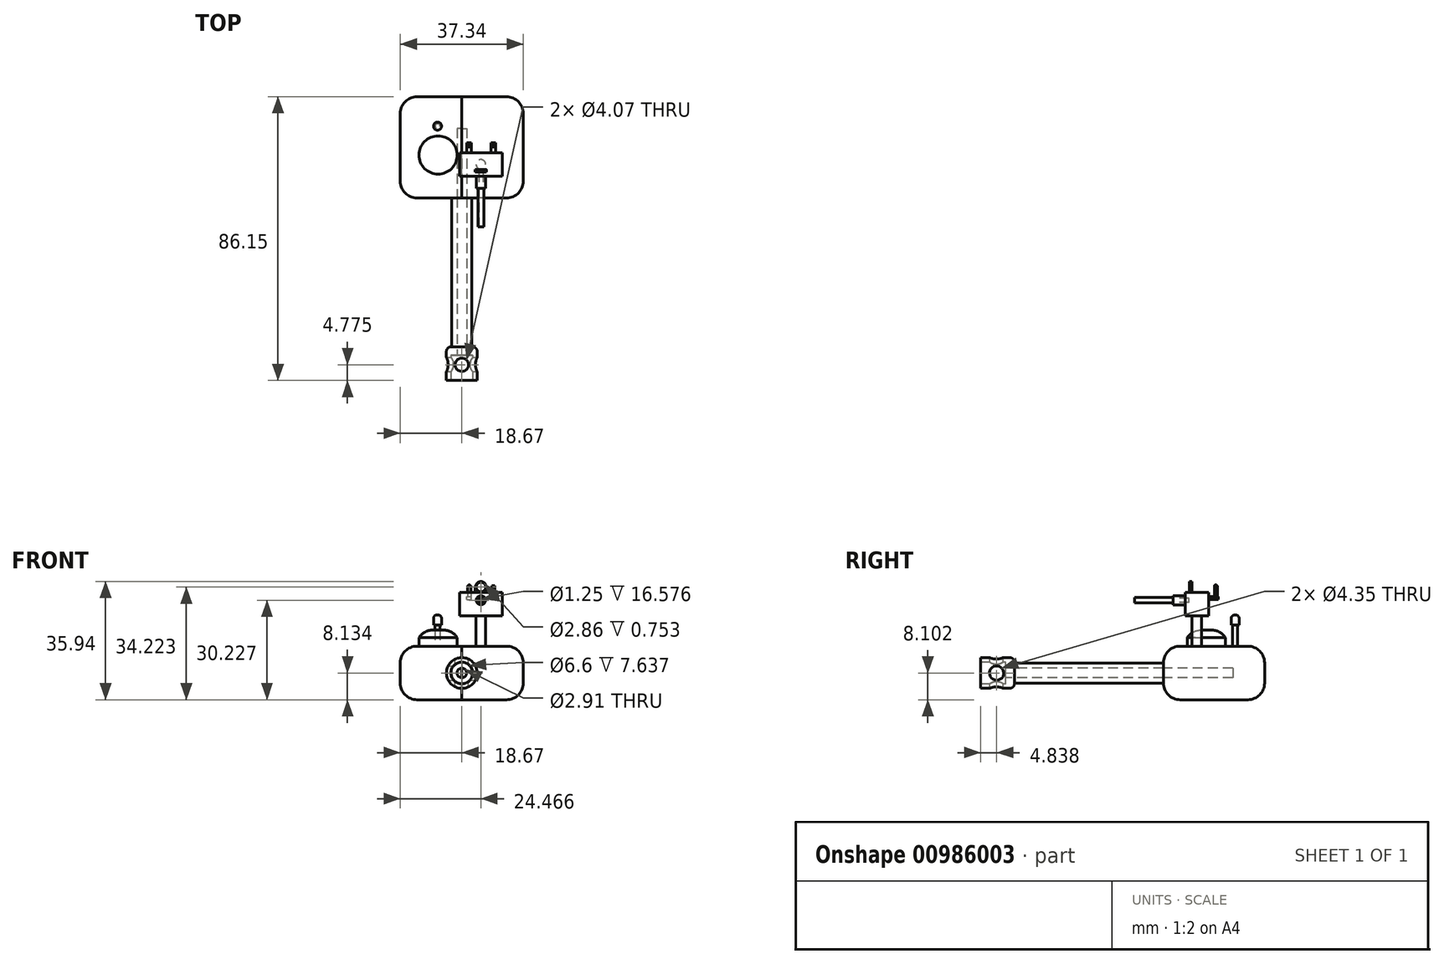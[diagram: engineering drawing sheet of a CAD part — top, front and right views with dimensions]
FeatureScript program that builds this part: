
annotation { "Feature Type Name" : "Feature", "Feature Type Description" : "" }
export const myFeature = defineFeature(function(context is Context, id is Id, definition is map)
    precondition{}
    {
        {
            var Q0;
            Q0=qCreatedBy(makeId("Top.planeOp"),FACE);
            var sketch = newSketch(context, id + "F0", { "sketchPlane" : qUnion([Q0])});
            skLineSegment(sketch, "E0.bottom", {"start": v(27.35, 36.84) * mm, "end": v(45.64, 36.84) * mm});
            skLineSegment(sketch, "E0.top", {"start": v(27.35, -37.1) * mm, "end": v(45.64, -37.1) * mm});
            skLineSegment(sketch, "E0.left", {"start": v(27.35, 36.84) * mm, "end": v(27.35, -37.1) * mm});
            skLineSegment(sketch, "E0.right", {"start": v(45.64, 36.84) * mm, "end": v(45.64, -37.1) * mm});
            skSolve(sketch);
        }
        {
            var Q0;
            Q0=makeQuery(id+"F0.imprint","IMPRINT",FACE,{"disambiguationData":[TD([[makeQuery(id+"F0.imprint","IMPRINT",EDGE,{"derivedFrom":sQuery(id+"F0.wireOp",EDGE,"E0.bottom")}),-1.0]])]});
            extrude(context, id + "F1", {"entities" : qUnion([Q0]), "depth" : 28.5 * mm, "offsetDistance" : 25.4 * mm});
        }
        {
            var Q0;
            Q0=makeQuery(id+"F1.opExtrude","SWEPT_FACE",FACE,{"disambiguationData":[OSD([sQuery(id+"F0.wireOp",EDGE,"E0.top")])]});
            extrude(context, id + "F2", {"entities" : qUnion([Q0]), "operationType" : NewBodyOperationType.ADD, "depth" : 18.17 * mm, "offsetDistance" : 25.4 * mm});
        }
        {
            var Q0;
            {var subQ0=sQuery(id+"F0.wireOp",EDGE,"E0.top");Q0=makeQuery(id+"F2.opExtrude","CAP_EDGE",EDGE,{"disambiguationData":[OSD([subQ0]),TDD([makeQuery(id+"F1.opExtrude","CAP_EDGE",EDGE,{"disambiguationData":[OSD([subQ0])],"isStart":true})])],"isStart":false});}
            var Q1;
            {var subQ0=sQuery(id+"F0.wireOp",EDGE,"E0.top");Q1=makeQuery(id+"F2.opExtrude","CAP_EDGE",EDGE,{"disambiguationData":[OSD([subQ0]),TDD([makeQuery(id+"F1.opExtrude","CAP_EDGE",EDGE,{"disambiguationData":[OSD([subQ0])],"isStart":false})])],"isStart":false});}
            fillet(context, id + "F3", {"entities" : qUnion([Q0, Q1]), "radius" : 16.42 * mm, "tangentPropagation" : true, "allowEdgeOverflow" : false});
        }
        {
            var Q0;
            Q0=makeQuery(id+"F1.opExtrude","SWEPT_BODY",BODY,{"disambiguationData":[OSD([sQuery(id+"F0.wireOp",EDGE,"E0.bottom"),sQuery(id+"F0.wireOp",EDGE,"E0.top"),sQuery(id+"F0.wireOp",EDGE,"E0.left"),sQuery(id+"F0.wireOp",EDGE,"E0.right")])]});
            var Q1;
            Q1=qCreatedBy(makeId("Front.planeOp"),FACE);
            mirror(context, id + "F4", {"operationType" : NewBodyOperationType.ADD, "entities" : qUnion([Q0]), "mirrorPlane" : qUnion([Q1])});
        }
        {
            var Q0;
            {var subQ0=sQuery(id+"F0.wireOp",EDGE,"E0.top");var subQ1=makeQuery(id+"F2.boolean.opBoolean","MERGE",FACE,{"derivedFrom":[makeQuery(id+"F1.opExtrude","CAP_FACE",FACE,{"disambiguationData":[OSD([sQuery(id+"F0.wireOp",EDGE,"E0.bottom"),subQ0,sQuery(id+"F0.wireOp",EDGE,"E0.left"),sQuery(id+"F0.wireOp",EDGE,"E0.right")])],"isStart":false}),makeQuery(id+"F2.opExtrude","SWEPT_FACE",FACE,{"disambiguationData":[OSD([subQ0]),TDD([makeQuery(id+"F1.opExtrude","CAP_EDGE",EDGE,{"disambiguationData":[OSD([subQ0])],"isStart":false})])]})]});Q0=makeQuery(id+"F4.boolean.opBoolean","MERGE",FACE,{"derivedFrom":[subQ1,makeQuery(id+"F4.opPattern","COPY",FACE,{"derivedFrom":subQ1,"instanceName":"1"})]});}
            var sketch = newSketch(context, id + "F5", { "sketchPlane" : qUnion([Q0])});
            skLineSegment(sketch, "E1.bottom", {"start": v(36.5, 38.84) * mm, "end": v(0, 38.84) * mm});
            skLineSegment(sketch, "E1.top", {"start": v(36.5, -38.84) * mm, "end": v(0, -38.84) * mm});
            skLineSegment(sketch, "E1.left", {"start": v(36.5, 38.84) * mm, "end": v(36.5, -38.84) * mm});
            skLineSegment(sketch, "E1.right", {"start": v(0, 38.84) * mm, "end": v(0, -38.84) * mm});
            skSolve(sketch);
        }
        {
            var Q0;
            {var subQ5=sQuery(id+"F5.wireOp",EDGE,"E1.right");Q0=makeQuery(id+"F5.imprint","IMPRINT",FACE,{"disambiguationData":[TD([[makeQuery(id+"F5.imprint","IMPRINT",EDGE,{"derivedFrom":subQ5}),1.0]])]});}
            var Q1;
            {var subQ5=sQuery(id+"F5.wireOp",EDGE,"E1.left");Q1=makeQuery(id+"F5.imprint","IMPRINT",FACE,{"disambiguationData":[TD([[makeQuery(id+"F5.imprint","IMPRINT",EDGE,{"derivedFrom":subQ5}),-1.0]])]});}
            extrude(context, id + "F6", {"entities" : qUnion([Q0, Q1]), "depth" : 15.55 * mm, "offsetDistance" : 25.4 * mm});
        }
        {
            var Q0;
            Q0=makeQuery(id+"F6.opExtrude","CAP_EDGE",EDGE,{"disambiguationData":[OSD([sQuery(id+"F5.wireOp",EDGE,"E1.top")])],"isStart":false});
            fillet(context, id + "F7", {"entities" : qUnion([Q0]), "radius" : 16.9 * mm, "tangentPropagation" : true, "allowEdgeOverflow" : false});
        }
        {
            var Q0;
            Q0=makeQuery(id+"F6.opExtrude","CAP_FACE",FACE,{"disambiguationData":[OSD([sQuery(id+"F5.wireOp",EDGE,"E1.bottom"),sQuery(id+"F5.wireOp",EDGE,"E1.top"),sQuery(id+"F5.wireOp",EDGE,"E1.left"),sQuery(id+"F5.wireOp",EDGE,"E1.right")])],"isStart":false});
            var sketch = newSketch(context, id + "F8", { "sketchPlane" : qUnion([Q0])});
            skLineSegment(sketch, "E2.bottom", {"start": v(36.5, 38.84) * mm, "end": v(0, 38.84) * mm});
            skLineSegment(sketch, "E2.top", {"start": v(36.5, 0) * mm, "end": v(0, 0) * mm});
            skLineSegment(sketch, "E2.left", {"start": v(36.5, 38.84) * mm, "end": v(36.5, 0) * mm});
            skLineSegment(sketch, "E2.right", {"start": v(0, 38.84) * mm, "end": v(0, 0) * mm});
            skSolve(sketch);
        }
        {
            var Q0;
            Q0=makeQuery(id+"F8.imprint","IMPRINT",FACE,{"disambiguationData":[TD([[makeQuery(id+"F8.imprint","IMPRINT",EDGE,{"derivedFrom":sQuery(id+"F8.wireOp",EDGE,"E2.bottom")}),1.0]])]});
            extrude(context, id + "F9", {"entities" : qUnion([Q0]), "operationType" : NewBodyOperationType.ADD, "depth" : 10.94 * mm, "offsetDistance" : 25.4 * mm});
        }
        {
            var Q0;
            Q0=makeQuery(id+"F9.opExtrude","CAP_EDGE",EDGE,{"disambiguationData":[OSD([sQuery(id+"F8.wireOp",EDGE,"E2.top")])],"isStart":false});
            fillet(context, id + "F10", {"entities" : qUnion([Q0]), "radius" : 179.02 * mm, "tangentPropagation" : true, "allowEdgeOverflow" : false});
        }
        {
            var Q0;
            Q0=makeQuery(id+"F10.opFillet","BLEND_EDGE",EDGE,{"blendedFrom":[makeQuery(id+"F9.opExtrude","CAP_EDGE",EDGE,{"disambiguationData":[OSD([sQuery(id+"F8.wireOp",EDGE,"E2.top")])],"isStart":false}),makeQuery(id+"F9.boolean.opBoolean","MERGE",FACE,{"derivedFrom":[makeQuery(id+"F6.opExtrude","SWEPT_FACE",FACE,{"disambiguationData":[OSD([sQuery(id+"F5.wireOp",EDGE,"E1.bottom")])]}),makeQuery(id+"F9.opExtrude","SWEPT_FACE",FACE,{"disambiguationData":[OSD([sQuery(id+"F8.wireOp",EDGE,"E2.bottom")])]})]})],"blendedInto":[makeQuery(id+"F9.boolean.opBoolean","MERGE",FACE,{"derivedFrom":[makeQuery(id+"F6.opExtrude","SWEPT_FACE",FACE,{"disambiguationData":[OSD([sQuery(id+"F5.wireOp",EDGE,"E1.bottom")])]}),makeQuery(id+"F9.opExtrude","SWEPT_FACE",FACE,{"disambiguationData":[OSD([sQuery(id+"F8.wireOp",EDGE,"E2.bottom")])]})]})]});
            fillet(context, id + "F11", {"entities" : qUnion([Q0]), "radius" : 28.97 * mm, "tangentPropagation" : true, "allowEdgeOverflow" : false});
        }
        {
            var Q0;
            Q0=makeQuery(id+"F7.opFillet","BLEND_EDGE",EDGE,{"blendedFrom":[makeQuery(id+"F6.opExtrude","CAP_EDGE",EDGE,{"disambiguationData":[OSD([sQuery(id+"F5.wireOp",EDGE,"E1.top")])],"isStart":false}),makeQuery(id+"F6.opExtrude","SWEPT_FACE",FACE,{"disambiguationData":[OSD([sQuery(id+"F5.wireOp",EDGE,"E1.left")])]})],"blendedInto":[makeQuery(id+"F6.opExtrude","SWEPT_FACE",FACE,{"disambiguationData":[OSD([sQuery(id+"F5.wireOp",EDGE,"E1.left")])]})]});
            var Q1;
            Q1=makeQuery(id+"F11.opFillet","BLEND_EDGE",EDGE,{"blendedFrom":[makeQuery(id+"F10.opFillet","BLEND_EDGE",EDGE,{"blendedFrom":[makeQuery(id+"F9.opExtrude","CAP_EDGE",EDGE,{"disambiguationData":[OSD([sQuery(id+"F8.wireOp",EDGE,"E2.top")])],"isStart":false}),makeQuery(id+"F9.boolean.opBoolean","MERGE",FACE,{"derivedFrom":[makeQuery(id+"F6.opExtrude","SWEPT_FACE",FACE,{"disambiguationData":[OSD([sQuery(id+"F5.wireOp",EDGE,"E1.bottom")])]}),makeQuery(id+"F9.opExtrude","SWEPT_FACE",FACE,{"disambiguationData":[OSD([sQuery(id+"F8.wireOp",EDGE,"E2.bottom")])]})]})],"blendedInto":[makeQuery(id+"F9.boolean.opBoolean","MERGE",FACE,{"derivedFrom":[makeQuery(id+"F6.opExtrude","SWEPT_FACE",FACE,{"disambiguationData":[OSD([sQuery(id+"F5.wireOp",EDGE,"E1.bottom")])]}),makeQuery(id+"F9.opExtrude","SWEPT_FACE",FACE,{"disambiguationData":[OSD([sQuery(id+"F8.wireOp",EDGE,"E2.bottom")])]})]})]}),makeQuery(id+"F9.boolean.opBoolean","MERGE",FACE,{"derivedFrom":[makeQuery(id+"F6.opExtrude","SWEPT_FACE",FACE,{"disambiguationData":[OSD([sQuery(id+"F5.wireOp",EDGE,"E1.left")])]}),makeQuery(id+"F9.opExtrude","SWEPT_FACE",FACE,{"disambiguationData":[OSD([sQuery(id+"F8.wireOp",EDGE,"E2.left")])]})]})],"blendedInto":[makeQuery(id+"F9.boolean.opBoolean","MERGE",FACE,{"derivedFrom":[makeQuery(id+"F6.opExtrude","SWEPT_FACE",FACE,{"disambiguationData":[OSD([sQuery(id+"F5.wireOp",EDGE,"E1.left")])]}),makeQuery(id+"F9.opExtrude","SWEPT_FACE",FACE,{"disambiguationData":[OSD([sQuery(id+"F8.wireOp",EDGE,"E2.left")])]})]})]});
            fillet(context, id + "F12", {"entities" : qUnion([Q0, Q1]), "radius" : 5.08 * mm, "tangentPropagation" : true, "allowEdgeOverflow" : false});
        }
        {
            var Q0;
            {var subQ0=sQuery(id+"F0.wireOp",EDGE,"E0.right");var subQ1=sQuery(id+"F0.wireOp",EDGE,"E0.top");Q0=makeQuery(id+"F4.opPattern","COPY",EDGE,{"derivedFrom":makeQuery(id+"F3.opFillet","BLEND_EDGE",EDGE,{"blendedFrom":[makeQuery(id+"F2.opExtrude","CAP_EDGE",EDGE,{"disambiguationData":[OSD([subQ1]),TDD([makeQuery(id+"F1.opExtrude","CAP_EDGE",EDGE,{"disambiguationData":[OSD([subQ1])],"isStart":false})])],"isStart":false}),makeQuery(id+"F2.boolean.opBoolean","MERGE",FACE,{"derivedFrom":[makeQuery(id+"F1.opExtrude","SWEPT_FACE",FACE,{"disambiguationData":[OSD([subQ0])]}),makeQuery(id+"F2.opExtrude","SWEPT_FACE",FACE,{"disambiguationData":[OSD([subQ1,subQ0])]})]})],"blendedInto":[makeQuery(id+"F2.boolean.opBoolean","MERGE",FACE,{"derivedFrom":[makeQuery(id+"F1.opExtrude","SWEPT_FACE",FACE,{"disambiguationData":[OSD([subQ0])]}),makeQuery(id+"F2.opExtrude","SWEPT_FACE",FACE,{"disambiguationData":[OSD([subQ1,subQ0])]})]})]}),"instanceName":"1"});}
            var Q1;
            {var subQ0=sQuery(id+"F0.wireOp",EDGE,"E0.right");var subQ1=sQuery(id+"F0.wireOp",EDGE,"E0.top");Q1=makeQuery(id+"F4.opPattern","COPY",EDGE,{"derivedFrom":makeQuery(id+"F3.opFillet","BLEND_EDGE",EDGE,{"blendedFrom":[makeQuery(id+"F2.opExtrude","CAP_EDGE",EDGE,{"disambiguationData":[OSD([subQ1]),TDD([makeQuery(id+"F1.opExtrude","CAP_EDGE",EDGE,{"disambiguationData":[OSD([subQ1])],"isStart":true})])],"isStart":false}),makeQuery(id+"F2.boolean.opBoolean","MERGE",FACE,{"derivedFrom":[makeQuery(id+"F1.opExtrude","SWEPT_FACE",FACE,{"disambiguationData":[OSD([subQ0])]}),makeQuery(id+"F2.opExtrude","SWEPT_FACE",FACE,{"disambiguationData":[OSD([subQ1,subQ0])]})]})],"blendedInto":[makeQuery(id+"F2.boolean.opBoolean","MERGE",FACE,{"derivedFrom":[makeQuery(id+"F1.opExtrude","SWEPT_FACE",FACE,{"disambiguationData":[OSD([subQ0])]}),makeQuery(id+"F2.opExtrude","SWEPT_FACE",FACE,{"disambiguationData":[OSD([subQ1,subQ0])]})]})]}),"instanceName":"1"});}
            fillet(context, id + "F13", {"entities" : qUnion([Q0, Q1]), "radius" : 5.08 * mm, "tangentPropagation" : true, "allowEdgeOverflow" : false});
        }
        {
            var Q0;
            {var subQ0=sQuery(id+"F0.wireOp",EDGE,"E0.left");var subQ1=sQuery(id+"F0.wireOp",EDGE,"E0.top");Q0=makeQuery(id+"F4.opPattern","COPY",EDGE,{"derivedFrom":makeQuery(id+"F3.opFillet","BLEND_EDGE",EDGE,{"blendedFrom":[makeQuery(id+"F2.opExtrude","CAP_EDGE",EDGE,{"disambiguationData":[OSD([subQ1]),TDD([makeQuery(id+"F1.opExtrude","CAP_EDGE",EDGE,{"disambiguationData":[OSD([subQ1])],"isStart":false})])],"isStart":false}),makeQuery(id+"F2.boolean.opBoolean","MERGE",FACE,{"derivedFrom":[makeQuery(id+"F1.opExtrude","SWEPT_FACE",FACE,{"disambiguationData":[OSD([subQ0])]}),makeQuery(id+"F2.opExtrude","SWEPT_FACE",FACE,{"disambiguationData":[OSD([subQ1,subQ0])]})]})],"blendedInto":[makeQuery(id+"F2.boolean.opBoolean","MERGE",FACE,{"derivedFrom":[makeQuery(id+"F1.opExtrude","SWEPT_FACE",FACE,{"disambiguationData":[OSD([subQ0])]}),makeQuery(id+"F2.opExtrude","SWEPT_FACE",FACE,{"disambiguationData":[OSD([subQ1,subQ0])]})]})]}),"instanceName":"1"});}
            var Q1;
            {var subQ0=sQuery(id+"F0.wireOp",EDGE,"E0.left");var subQ1=sQuery(id+"F0.wireOp",EDGE,"E0.top");Q1=makeQuery(id+"F4.opPattern","COPY",EDGE,{"derivedFrom":makeQuery(id+"F3.opFillet","BLEND_EDGE",EDGE,{"blendedFrom":[makeQuery(id+"F2.opExtrude","CAP_EDGE",EDGE,{"disambiguationData":[OSD([subQ1]),TDD([makeQuery(id+"F1.opExtrude","CAP_EDGE",EDGE,{"disambiguationData":[OSD([subQ1])],"isStart":true})])],"isStart":false}),makeQuery(id+"F2.boolean.opBoolean","MERGE",FACE,{"derivedFrom":[makeQuery(id+"F1.opExtrude","SWEPT_FACE",FACE,{"disambiguationData":[OSD([subQ0])]}),makeQuery(id+"F2.opExtrude","SWEPT_FACE",FACE,{"disambiguationData":[OSD([subQ1,subQ0])]})]})],"blendedInto":[makeQuery(id+"F2.boolean.opBoolean","MERGE",FACE,{"derivedFrom":[makeQuery(id+"F1.opExtrude","SWEPT_FACE",FACE,{"disambiguationData":[OSD([subQ0])]}),makeQuery(id+"F2.opExtrude","SWEPT_FACE",FACE,{"disambiguationData":[OSD([subQ1,subQ0])]})]})]}),"instanceName":"1"});}
            fillet(context, id + "F14", {"entities" : qUnion([Q0, Q1]), "radius" : 5.08 * mm, "tangentPropagation" : true, "allowEdgeOverflow" : false});
        }
        {
            var Q0;
            Q0=qCreatedBy(makeId("Top.planeOp"),FACE);
            cPlane(context, id + "F15", {"entities" : qUnion([Q0]), "cplaneType" : CPlaneType.OFFSET, "offset" : 47.5 * mm, "width" : 152.4 * mm, "height" : 152.4 * mm});
        }
        {
            var Q0;
            Q0=qCreatedBy(id+"F15.planeOp",FACE);
            var sketch = newSketch(context, id + "F16", { "sketchPlane" : qUnion([Q0])});
            skLineSegment(sketch, "E3.bottom", {"start": v(18.67, -10.17) * mm, "end": v(0, -10.17) * mm});
            skLineSegment(sketch, "E3.top", {"start": v(18.67, 20.54) * mm, "end": v(0, 20.54) * mm});
            skLineSegment(sketch, "E3.left", {"start": v(18.67, -10.17) * mm, "end": v(18.67, 20.54) * mm});
            skLineSegment(sketch, "E3.right", {"start": v(0, -10.17) * mm, "end": v(0, 20.54) * mm});
            skSolve(sketch);
        }
        {
            var Q0;
            Q0=makeQuery(id+"F16.imprint","IMPRINT",FACE,{"disambiguationData":[TD([[makeQuery(id+"F16.imprint","IMPRINT",EDGE,{"derivedFrom":sQuery(id+"F16.wireOp",EDGE,"E3.bottom")}),-1.0]])]});
            extrude(context, id + "F17", {"entities" : qUnion([Q0]), "depth" : 16.27 * mm, "offsetDistance" : 25.4 * mm});
        }
        {
            var Q0;
            Q0=makeQuery(id+"F17.opExtrude","CAP_EDGE",EDGE,{"disambiguationData":[OSD([sQuery(id+"F16.wireOp",EDGE,"E3.left")])],"isStart":false});
            var Q1;
            Q1=makeQuery(id+"F17.opExtrude","SWEPT_EDGE",EDGE,{"disambiguationData":[OSD([sQuery(id+"F16.wireOp",EDGE,"E3.top"),sQuery(id+"F16.wireOp",EDGE,"E3.left")])]});
            var Q2;
            Q2=makeQuery(id+"F17.opExtrude","CAP_EDGE",EDGE,{"disambiguationData":[OSD([sQuery(id+"F16.wireOp",EDGE,"E3.left")])],"isStart":true});
            var Q3;
            Q3=makeQuery(id+"F17.opExtrude","SWEPT_EDGE",EDGE,{"disambiguationData":[OSD([sQuery(id+"F16.wireOp",EDGE,"E3.bottom"),sQuery(id+"F16.wireOp",EDGE,"E3.left")])]});
            var Q4;
            Q4=makeQuery(id+"F17.opExtrude","CAP_EDGE",EDGE,{"disambiguationData":[OSD([sQuery(id+"F16.wireOp",EDGE,"E3.top")])],"isStart":false});
            var Q5;
            Q5=makeQuery(id+"F17.opExtrude","CAP_EDGE",EDGE,{"disambiguationData":[OSD([sQuery(id+"F16.wireOp",EDGE,"E3.top")])],"isStart":true});
            var Q6;
            Q6=makeQuery(id+"F17.opExtrude","CAP_EDGE",EDGE,{"disambiguationData":[OSD([sQuery(id+"F16.wireOp",EDGE,"E3.bottom")])],"isStart":false});
            var Q7;
            Q7=makeQuery(id+"F17.opExtrude","CAP_EDGE",EDGE,{"disambiguationData":[OSD([sQuery(id+"F16.wireOp",EDGE,"E3.bottom")])],"isStart":true});
            fillet(context, id + "F18", {"entities" : qUnion([Q0, Q1, Q2, Q3, Q4, Q5, Q6, Q7]), "radius" : 5.08 * mm, "tangentPropagation" : true, "allowEdgeOverflow" : false});
        }
        {
            var Q0;
            Q0=makeQuery(id+"F17.opExtrude","SWEPT_BODY",BODY,{"disambiguationData":[OSD([sQuery(id+"F16.wireOp",EDGE,"E3.bottom"),sQuery(id+"F16.wireOp",EDGE,"E3.top"),sQuery(id+"F16.wireOp",EDGE,"E3.left"),sQuery(id+"F16.wireOp",EDGE,"E3.right")])]});
            var Q1;
            Q1=makeQuery(id+"F6.opExtrude","SWEPT_BODY",BODY,{"disambiguationData":[OSD([sQuery(id+"F5.wireOp",EDGE,"E1.bottom"),sQuery(id+"F5.wireOp",EDGE,"E1.top"),sQuery(id+"F5.wireOp",EDGE,"E1.left"),sQuery(id+"F5.wireOp",EDGE,"E1.right")])]});
            var Q2;
            Q2=makeQuery(id+"F1.opExtrude","SWEPT_BODY",BODY,{"disambiguationData":[OSD([sQuery(id+"F0.wireOp",EDGE,"E0.bottom"),sQuery(id+"F0.wireOp",EDGE,"E0.top"),sQuery(id+"F0.wireOp",EDGE,"E0.left"),sQuery(id+"F0.wireOp",EDGE,"E0.right")])]});
            var Q3;
            Q3=qCreatedBy(makeId("Right.planeOp"),FACE);
            mirror(context, id + "F19", {"entities" : qUnion([Q0, Q1, Q2]), "mirrorPlane" : qUnion([Q3])});
        }
        {
            var Q0;
            Q0=makeQuery(id+"F17.opExtrude","SWEPT_FACE",FACE,{"disambiguationData":[OSD([sQuery(id+"F16.wireOp",EDGE,"E3.bottom")])]});
            var sketch = newSketch(context, id + "F20", { "sketchPlane" : qUnion([Q0])});
            skCircle(sketch, "E4", {"center": v(0, 55.64) * mm, "radius": 3.06 * mm});
            skSolve(sketch);
        }
        {
            var Q0;
            {var subQ1=sQuery(id+"F16.wireOp",EDGE,"E3.bottom");var subQ3=makeQuery(id+"F17.opExtrude","SWEPT_EDGE",EDGE,{"disambiguationData":[OSD([subQ1,sQuery(id+"F16.wireOp",EDGE,"E3.right")])]});Q0=makeQuery(id+"F20.imprint","IMPRINT",FACE,{"disambiguationData":[TD([[makeQuery(id+"F20.imprint","IMPRINT",EDGE,{"derivedFrom":subQ3}),-1.0]])]});}
            var Q1;
            {var subQ1=sQuery(id+"F16.wireOp",EDGE,"E3.bottom");var subQ3=makeQuery(id+"F17.opExtrude","SWEPT_EDGE",EDGE,{"disambiguationData":[OSD([subQ1,sQuery(id+"F16.wireOp",EDGE,"E3.right")])]});Q1=makeQuery(id+"F20.imprint","IMPRINT",FACE,{"disambiguationData":[TD([[makeQuery(id+"F20.imprint","IMPRINT",EDGE,{"derivedFrom":subQ3}),1.0]])]});}
            extrude(context, id + "F21", {"entities" : qUnion([Q0, Q1]), "depth" : 45.2 * mm, "offsetDistance" : 25.4 * mm});
        }
        {
            var Q0;
            Q0=makeQuery(id+"F21.opExtrude","CAP_FACE",FACE,{"disambiguationData":[OSD([sQuery(id+"F20.wireOp",EDGE,"E4")])],"isStart":false});
            var sketch = newSketch(context, id + "F22", { "sketchPlane" : qUnion([Q0])});
            skCircle(sketch, "E5", {"center": v(0, 55.64) * mm, "radius": 4.67 * mm});
            skSolve(sketch);
        }
        {
            var Q0;
            Q0=qSketchRegion(id+"F22",true);
            extrude(context, id + "F23", {"entities" : qUnion([Q0]), "operationType" : NewBodyOperationType.ADD, "depth" : 10.23 * mm, "offsetDistance" : 25.4 * mm});
        }
        {
            var Q0;
            Q0=makeQuery(id+"F23.opExtrude","CAP_FACE",FACE,{"disambiguationData":[OSD([sQuery(id+"F22.wireOp",EDGE,"E5")])],"isStart":false});
            var sketch = newSketch(context, id + "F24", { "sketchPlane" : qUnion([Q0])});
            skCircle(sketch, "E6", {"center": v(0, 55.64) * mm, "radius": 3.3 * mm});
            skSolve(sketch);
        }
        {
            var Q0;
            Q0=qSketchRegion(id+"F24",true);
            extrude(context, id + "F25", {"entities" : qUnion([Q0]), "operationType" : NewBodyOperationType.REMOVE, "oppositeDirection" : true, "depth" : 7.64 * mm, "offsetDistance" : 25.4 * mm});
        }
        {
            var Q0;
            Q0=makeQuery(id+"F25.boolean.opBoolean","COPY",FACE,{"derivedFrom":makeQuery(id+"F25.opExtrude","CAP_FACE",FACE,{"disambiguationData":[OSD([sQuery(id+"F24.wireOp",EDGE,"E6")])],"isStart":false})});
            var sketch = newSketch(context, id + "F26", { "sketchPlane" : qUnion([Q0])});
            skCircle(sketch, "E7", {"center": v(0, 55.64) * mm, "radius": 1.45 * mm});
            skSolve(sketch);
        }
        {
            var Q0;
            Q0=qSketchRegion(id+"F26",true);
            extrude(context, id + "F27", {"entities" : qUnion([Q0]), "operationType" : NewBodyOperationType.REMOVE, "oppositeDirection" : true, "depth" : 68.9 * mm, "offsetDistance" : 25.4 * mm});
        }
        {
            var Q0;
            Q0=qCreatedBy(id+"F15.planeOp",FACE);
            var sketch = newSketch(context, id + "F28", { "sketchPlane" : qUnion([Q0])});
            skCircle(sketch, "E8", {"center": v(0, 0) * mm, "radius": 4.47 * mm});
            skSolve(sketch);
        }
        {
            var Q0;
            Q0=qSketchRegion(id+"F28",true);
            extrude(context, id + "F29", {"entities" : qUnion([Q0]), "oppositeDirection" : true, "depth" : 11.7 * mm, "offsetDistance" : 25.4 * mm});
        }
        {
            var Q0;
            Q0=qCreatedBy(makeId("Front.planeOp"),FACE);
            var sketch = newSketch(context, id + "F30", { "sketchPlane" : qUnion([Q0])});
            skCircle(sketch, "E9", {"center": v(18.82, 31.85) * mm, "radius": 2.62 * mm});
            skSolve(sketch);
        }
        {
            var Q0;
            Q0=qSketchRegion(id+"F30",true);
            extrude(context, id + "F31", {"entities" : qUnion([Q0]), "operationType" : NewBodyOperationType.ADD, "oppositeDirection" : true, "depth" : 44.92 * mm, "offsetDistance" : 25.4 * mm});
        }
        {
            var Q0;
            Q0=makeQuery(id+"F31.opExtrude","CAP_FACE",FACE,{"disambiguationData":[OSD([sQuery(id+"F30.wireOp",EDGE,"E9")])],"isStart":false});
            var sketch = newSketch(context, id + "F32", { "sketchPlane" : qUnion([Q0])});
            skCircle(sketch, "E10", {"center": v(-18.82, 31.85) * mm, "radius": 1.78 * mm});
            skSolve(sketch);
        }
        {
            var Q0;
            Q0=makeQuery(id+"F32.imprint","IMPRINT",FACE,{"disambiguationData":[TD([[makeQuery(id+"F32.imprint","IMPRINT",EDGE,{"derivedFrom":sQuery(id+"F32.wireOp",EDGE,"E10")}),1.0]])]});
            extrude(context, id + "F33", {"entities" : qUnion([Q0]), "operationType" : NewBodyOperationType.REMOVE, "oppositeDirection" : true, "depth" : 40.22 * mm, "offsetDistance" : 25.4 * mm});
        }
        {
            var Q0;
            Q0=makeQuery(id+"F19.opPattern","COPY",FACE,{"derivedFrom":makeQuery(id+"F17.opExtrude","CAP_FACE",FACE,{"disambiguationData":[OSD([sQuery(id+"F16.wireOp",EDGE,"E3.bottom"),sQuery(id+"F16.wireOp",EDGE,"E3.top"),sQuery(id+"F16.wireOp",EDGE,"E3.left"),sQuery(id+"F16.wireOp",EDGE,"E3.right")])],"isStart":false}),"instanceName":"1"});
            var sketch = newSketch(context, id + "F34", { "sketchPlane" : qUnion([Q0])});
            skSolve(sketch);
        }
        {
            var Q0;
            {var subQ0=sQuery(id+"F16.wireOp",EDGE,"E3.right");Q0=makeQuery(id+"F34.imprint","IMPRINT",FACE,{"disambiguationData":[TD([[makeQuery(id+"F34.imprint","IMPRINT",EDGE,{"derivedFrom":makeQuery(id+"F19.opPattern","COPY",EDGE,{"derivedFrom":makeQuery(id+"F17.opExtrude","CAP_EDGE",EDGE,{"disambiguationData":[OSD([subQ0])],"isStart":false}),"instanceName":"1"})}),1.0]])]});}
            var sketch = newSketch(context, id + "F35", { "sketchPlane" : qUnion([Q0])});
            skCircle(sketch, "E11", {"center": v(-7.38, 11.62) * mm, "radius": 0.74 * mm});
            skSolve(sketch);
        }
        {
            var Q0;
            Q0=qSketchRegion(id+"F35",true);
            extrude(context, id + "F36", {"entities" : qUnion([Q0]), "operationType" : NewBodyOperationType.ADD, "depth" : 6.46 * mm, "offsetDistance" : 25.4 * mm});
        }
        {
            var Q0;
            Q0=makeQuery(id+"F36.opExtrude","CAP_FACE",FACE,{"disambiguationData":[OSD([sQuery(id+"F35.wireOp",EDGE,"E11")])],"isStart":false});
            var sketch = newSketch(context, id + "F37", { "sketchPlane" : qUnion([Q0])});
            skCircle(sketch, "E12", {"center": v(-7.38, 11.62) * mm, "radius": 1.21 * mm});
            skSolve(sketch);
        }
        {
            var Q0;
            Q0=qSketchRegion(id+"F37",true);
            extrude(context, id + "F38", {"entities" : qUnion([Q0]), "operationType" : NewBodyOperationType.ADD, "depth" : 3.02 * mm, "offsetDistance" : 25.4 * mm});
        }
        {
            var Q0;
            Q0=makeQuery(id+"F1.opExtrude","SWEPT_BODY",BODY,{"disambiguationData":[OSD([sQuery(id+"F0.wireOp",EDGE,"E0.bottom"),sQuery(id+"F0.wireOp",EDGE,"E0.top"),sQuery(id+"F0.wireOp",EDGE,"E0.left"),sQuery(id+"F0.wireOp",EDGE,"E0.right")])]});
            var Q1;
            Q1=makeQuery(id+"F19.opPattern","COPY",BODY,{"derivedFrom":makeQuery(id+"F1.opExtrude","SWEPT_BODY",BODY,{"disambiguationData":[OSD([sQuery(id+"F0.wireOp",EDGE,"E0.bottom"),sQuery(id+"F0.wireOp",EDGE,"E0.top"),sQuery(id+"F0.wireOp",EDGE,"E0.left"),sQuery(id+"F0.wireOp",EDGE,"E0.right")])]}),"instanceName":"1"});
            var Q2;
            Q2=makeQuery(id+"F19.opPattern","COPY",BODY,{"derivedFrom":makeQuery(id+"F6.opExtrude","SWEPT_BODY",BODY,{"disambiguationData":[OSD([sQuery(id+"F5.wireOp",EDGE,"E1.bottom"),sQuery(id+"F5.wireOp",EDGE,"E1.top"),sQuery(id+"F5.wireOp",EDGE,"E1.left"),sQuery(id+"F5.wireOp",EDGE,"E1.right")])]}),"instanceName":"1"});
            var Q3;
            Q3=makeQuery(id+"F6.opExtrude","SWEPT_BODY",BODY,{"disambiguationData":[OSD([sQuery(id+"F5.wireOp",EDGE,"E1.bottom"),sQuery(id+"F5.wireOp",EDGE,"E1.top"),sQuery(id+"F5.wireOp",EDGE,"E1.left"),sQuery(id+"F5.wireOp",EDGE,"E1.right")])]});
            var Q4;
            Q4=makeQuery(id+"F29.opExtrude","SWEPT_BODY",BODY,{"disambiguationData":[OSD([sQuery(id+"F28.wireOp",EDGE,"E8")])]});
            deleteBodies(context, id + "F39", {"entities" : qUnion([Q0, Q1, Q2, Q3, Q4])});
        }
        {
            var Q0;
            Q0=makeQuery(id+"F17.opExtrude","CAP_FACE",FACE,{"disambiguationData":[OSD([sQuery(id+"F16.wireOp",EDGE,"E3.bottom"),sQuery(id+"F16.wireOp",EDGE,"E3.top"),sQuery(id+"F16.wireOp",EDGE,"E3.left"),sQuery(id+"F16.wireOp",EDGE,"E3.right")])],"isStart":false});
            var sketch = newSketch(context, id + "F40", { "sketchPlane" : qUnion([Q0])});
            skSolve(sketch);
        }
        {
            var Q0;
            {var subQ0=sQuery(id+"F16.wireOp",EDGE,"E3.right");Q0=makeQuery(id+"F40.imprint","IMPRINT",FACE,{"disambiguationData":[TD([[makeQuery(id+"F40.imprint","IMPRINT",EDGE,{"derivedFrom":makeQuery(id+"F17.opExtrude","CAP_EDGE",EDGE,{"disambiguationData":[OSD([subQ0])],"isStart":false})}),-1.0]])]});}
            var sketch = newSketch(context, id + "F41", { "sketchPlane" : qUnion([Q0])});
            skCircle(sketch, "E13", {"center": v(5.8, 0) * mm, "radius": 1.46 * mm});
            skSolve(sketch);
        }
        {
            var Q0;
            Q0=makeQuery(id+"F41.imprint","IMPRINT",FACE,{"disambiguationData":[TD([[makeQuery(id+"F41.imprint","IMPRINT",EDGE,{"derivedFrom":sQuery(id+"F41.wireOp",EDGE,"E13")}),1.0]])]});
            extrude(context, id + "F42", {"entities" : qUnion([Q0]), "operationType" : NewBodyOperationType.ADD, "depth" : 9.17 * mm, "offsetDistance" : 25.4 * mm});
        }
        {
            var Q0;
            Q0=makeQuery(id+"F42.opExtrude","CAP_FACE",FACE,{"disambiguationData":[OSD([sQuery(id+"F41.wireOp",EDGE,"E13")])],"isStart":false});
            var sketch = newSketch(context, id + "F43", { "sketchPlane" : qUnion([Q0])});
            skLineSegment(sketch, "E14.bottom", {"start": v(12.26, 3.53) * mm, "end": v(-0.67, 3.53) * mm});
            skLineSegment(sketch, "E14.top", {"start": v(12.26, -3.53) * mm, "end": v(-0.67, -3.53) * mm});
            skLineSegment(sketch, "E14.left", {"start": v(12.26, 3.53) * mm, "end": v(12.26, -3.53) * mm});
            skLineSegment(sketch, "E14.right", {"start": v(-0.67, 3.53) * mm, "end": v(-0.67, -3.53) * mm});
            skPoint(sketch, "E14.middle", {"position": v(5.8, 0) * mm});
            skSolve(sketch);
        }
        {
            var Q0;
            Q0=makeQuery(id+"F43.imprint","IMPRINT",FACE,{"disambiguationData":[TD([[makeQuery(id+"F43.imprint","IMPRINT",EDGE,{"derivedFrom":sQuery(id+"F43.wireOp",EDGE,"E14.bottom")}),1.0]])]});
            var Q1;
            Q1=makeQuery(id+"F43.imprint","IMPRINT",FACE,{"disambiguationData":[TD([[makeQuery(id+"F43.imprint","IMPRINT",EDGE,{"derivedFrom":makeQuery(id+"F42.opExtrude","CAP_EDGE",EDGE,{"disambiguationData":[OSD([sQuery(id+"F41.wireOp",EDGE,"E13")])],"isStart":false})}),1.0]])]});
            extrude(context, id + "F44", {"entities" : qUnion([Q0, Q1]), "operationType" : NewBodyOperationType.ADD, "depth" : 7.14 * mm, "offsetDistance" : 25.4 * mm});
        }
        {
            var Q0;
            Q0=makeQuery(id+"F44.opExtrude","SWEPT_FACE",FACE,{"disambiguationData":[OSD([sQuery(id+"F43.wireOp",EDGE,"E14.top")])]});
            var sketch = newSketch(context, id + "F45", { "sketchPlane" : qUnion([Q0])});
            skCircle(sketch, "E15", {"center": v(5.8, 77.74) * mm, "radius": 1.38 * mm});
            skPoint(sketch, "E15.centerSnap0", {"position": v(5.8, 72.95) * mm});
            skSolve(sketch);
        }
        {
            var Q0;
            Q0=makeQuery(id+"F45.imprint","IMPRINT",FACE,{"disambiguationData":[TD([[makeQuery(id+"F45.imprint","IMPRINT",EDGE,{"derivedFrom":sQuery(id+"F45.wireOp",EDGE,"E15")}),1.0]])]});
            extrude(context, id + "F46", {"entities" : qUnion([Q0]), "operationType" : NewBodyOperationType.ADD, "depth" : 3.75 * mm, "offsetDistance" : 25.4 * mm});
        }
        {
            var Q0;
            Q0=makeQuery(id+"F46.opExtrude","CAP_FACE",FACE,{"disambiguationData":[OSD([sQuery(id+"F45.wireOp",EDGE,"E15")])],"isStart":false});
            var sketch = newSketch(context, id + "F47", { "sketchPlane" : qUnion([Q0])});
            skCircle(sketch, "E16", {"center": v(5.8, 77.74) * mm, "radius": 0.86 * mm});
            skSolve(sketch);
        }
        {
            var Q0;
            Q0 = qSketchRegion(id + "F47", true);
            extrude(context, id + "F48", {"entities" : qUnion([Q0]), "operationType" : NewBodyOperationType.ADD, "depth" : 11.66 * mm, "offsetDistance" : 25.4 * mm});
        }
        {
            var Q0;
            Q0=makeQuery(id+"F44.opExtrude","SWEPT_FACE",FACE,{"disambiguationData":[OSD([sQuery(id+"F43.wireOp",EDGE,"E14.bottom")])]});
            var sketch = newSketch(context, id + "F49", { "sketchPlane" : qUnion([Q0])});
            skLineSegment(sketch, "E17.bottom", {"start": v(-8.85, 77.98) * mm, "end": v(-10.23, 77.98) * mm});
            skLineSegment(sketch, "E17.top", {"start": v(-8.85, 78.87) * mm, "end": v(-10.23, 78.87) * mm});
            skLineSegment(sketch, "E17.left", {"start": v(-8.85, 77.98) * mm, "end": v(-8.85, 78.87) * mm});
            skLineSegment(sketch, "E17.right", {"start": v(-10.23, 77.98) * mm, "end": v(-10.23, 78.87) * mm});
            skPoint(sketch, "E17.middle", {"position": v(-9.54, 78.42) * mm});
            skLineSegment(sketch, "E18.bottom", {"start": v(-1.56, 77.98) * mm, "end": v(-2.9, 77.98) * mm});
            skLineSegment(sketch, "E18.top", {"start": v(-1.56, 78.87) * mm, "end": v(-2.9, 78.87) * mm});
            skLineSegment(sketch, "E18.left", {"start": v(-1.56, 77.98) * mm, "end": v(-1.56, 78.87) * mm});
            skLineSegment(sketch, "E18.right", {"start": v(-2.9, 77.98) * mm, "end": v(-2.9, 78.87) * mm});
            skPoint(sketch, "E18.middle", {"position": v(-2.23, 78.42) * mm});
            skPoint(sketch, "E18.middle.positionSnap0", {"position": v(-8.85, 78.42) * mm});
            skPoint(sketch, "E18.centerSnap0", {"position": v(-8.85, 78.42) * mm});
            skSolve(sketch);
        }
        {
            var Q0;
            Q0 = qSketchRegion(id + "F49", true);
            extrude(context, id + "F50", {"entities" : qUnion([Q0]), "operationType" : NewBodyOperationType.ADD, "depth" : 3.02 * mm, "offsetDistance" : 25.4 * mm});
        }
        {
            var Q0;
            Q0=makeQuery(id+"F50.opExtrude","SWEPT_FACE",FACE,{"disambiguationData":[OSD([sQuery(id+"F49.wireOp",EDGE,"E17.top")])]});
            var sketch = newSketch(context, id + "F51", { "sketchPlane" : qUnion([Q0])});
            skCircle(sketch, "E19", {"center": v(9.54, 5.76) * mm, "radius": 0.47 * mm});
            skPoint(sketch, "E19.centerSnap0", {"position": v(9.54, 6.55) * mm});
            skCircle(sketch, "E20", {"center": v(2.26, 5.76) * mm, "radius": 0.47 * mm});
            skSolve(sketch);
        }
        {
            var Q0;
            Q0=makeQuery(id+"F51.imprint","IMPRINT",FACE,{"disambiguationData":[TD([[makeQuery(id+"F51.imprint","IMPRINT",EDGE,{"derivedFrom":sQuery(id+"F51.wireOp",EDGE,"E20")}),1.0]])]});
            var Q1;
            Q1=makeQuery(id+"F51.imprint","IMPRINT",FACE,{"disambiguationData":[TD([[makeQuery(id+"F51.imprint","IMPRINT",EDGE,{"derivedFrom":sQuery(id+"F51.wireOp",EDGE,"E19")}),1.0]])]});
            extrude(context, id + "F52", {"entities" : qUnion([Q0, Q1]), "operationType" : NewBodyOperationType.ADD, "depth" : 3.3 * mm, "offsetDistance" : 25.4 * mm});
        }
        {
            var Q0;
            Q0=makeQuery(id+"F52.opExtrude","CAP_FACE",FACE,{"disambiguationData":[OSD([sQuery(id+"F51.wireOp",EDGE,"E20")])],"isStart":false});
            var sketch = newSketch(context, id + "F53", { "sketchPlane" : qUnion([Q0])});
            skCircle(sketch, "E21", {"center": v(2.26, 5.76) * mm, "radius": 0.27 * mm});
            skSolve(sketch);
        }
        {
            var Q0;
            Q0=makeQuery(id+"F53.imprint","IMPRINT",FACE,{"disambiguationData":[TD([[makeQuery(id+"F53.imprint","IMPRINT",EDGE,{"derivedFrom":sQuery(id+"F53.wireOp",EDGE,"E21")}),1.0]])]});
            extrude(context, id + "F54", {"entities" : qUnion([Q0]), "depth" : 0.26 * mm, "offsetDistance" : 25.4 * mm});
        }
        {
            var Q0;
            Q0=makeQuery(id+"F48.opExtrude","CAP_FACE",FACE,{"disambiguationData":[OSD([sQuery(id+"F47.wireOp",EDGE,"E16")])],"isStart":false});
            var sketch = newSketch(context, id + "F55", { "sketchPlane" : qUnion([Q0])});
            skCircle(sketch, "E22", {"center": v(5.8, 77.74) * mm, "radius": 0.62 * mm});
            skSolve(sketch);
        }
        {
            var Q0;
            Q0 = qSketchRegion(id + "F55", true);
            extrude(context, id + "F56", {"entities" : qUnion([Q0]), "operationType" : NewBodyOperationType.REMOVE, "oppositeDirection" : true, "depth" : 16.58 * mm, "offsetDistance" : 25.4 * mm});
        }
        {
            var Q0;
            Q0=qCreatedBy(id+"F15.planeOp",FACE);
            cPlane(context, id + "F57", {"entities" : qUnion([Q0]), "cplaneType" : CPlaneType.OFFSET, "offset" : 13.22 * mm, "width" : 152.4 * mm, "height" : 152.4 * mm});
        }
        {
            var Q0;
            Q0=qCreatedBy(id+"F57.planeOp",FACE);
            var sketch = newSketch(context, id + "F58", { "sketchPlane" : qUnion([Q0])});
            skCircle(sketch, "E23", {"center": v(0, -60.83) * mm, "radius": 2.04 * mm});
            skSolve(sketch);
        }
        {
            var Q0;
            Q0 = qSketchRegion(id + "F58", true);
            extrude(context, id + "F59", {"entities" : qUnion([Q0]), "operationType" : NewBodyOperationType.REMOVE, "oppositeDirection" : true, "depth" : 44.95 * mm, "offsetDistance" : 25.4 * mm});
        }
        {
            var Q0;
            Q0=qCreatedBy(makeId("Right.planeOp"),FACE);
            cPlane(context, id + "F60", {"entities" : qUnion([Q0]), "cplaneType" : CPlaneType.OFFSET, "offset" : 5.56 * mm, "width" : 152.4 * mm, "height" : 152.4 * mm});
        }
        {
            var Q0;
            Q0=qCreatedBy(id+"F60.planeOp",FACE);
            var sketch = newSketch(context, id + "F61", { "sketchPlane" : qUnion([Q0])});
            skCircle(sketch, "E24", {"center": v(-60.77, 55.61) * mm, "radius": 2.18 * mm});
            skSolve(sketch);
        }
        {
            var Q0;
            Q0=makeQuery(id+"F61.imprint","IMPRINT",FACE,{"disambiguationData":[TD([[makeQuery(id+"F61.imprint","IMPRINT",EDGE,{"derivedFrom":sQuery(id+"F61.wireOp",EDGE,"E24")}),1.0]])]});
            extrude(context, id + "F62", {"entities" : qUnion([Q0]), "operationType" : NewBodyOperationType.REMOVE, "oppositeDirection" : true, "depth" : 41.96 * mm, "offsetDistance" : 25.4 * mm});
        }
        {
            var Q0;
            Q0=makeQuery(id+"F23.opExtrude","CAP_EDGE",EDGE,{"disambiguationData":[OSD([sQuery(id+"F22.wireOp",EDGE,"E5")])],"isStart":true});
            fillet(context, id + "F63", {"entities" : qUnion([Q0]), "radius" : 1.43 * mm, "tangentPropagation" : true, "allowEdgeOverflow" : false});
        }
        {
            var Q0;
            Q0=makeQuery(id+"F38.opExtrude","CAP_EDGE",EDGE,{"disambiguationData":[OSD([sQuery(id+"F37.wireOp",EDGE,"E12")])],"isStart":false});
            fillet(context, id + "F64", {"entities" : qUnion([Q0]), "radius" : 1.05 * mm, "tangentPropagation" : true, "allowEdgeOverflow" : false});
        }
        {
            var Q0;
            Q0=makeQuery(id+"F44.opExtrude","CAP_FACE",FACE,{"disambiguationData":[OSD([sQuery(id+"F43.wireOp",EDGE,"E14.bottom"),sQuery(id+"F43.wireOp",EDGE,"E14.top"),sQuery(id+"F43.wireOp",EDGE,"E14.left"),sQuery(id+"F43.wireOp",EDGE,"E14.right")])],"isStart":false});
            var sketch = newSketch(context, id + "F65", { "sketchPlane" : qUnion([Q0])});
            skLineSegment(sketch, "E25.bottom", {"start": v(7.52, -1.56) * mm, "end": v(4.07, -1.56) * mm});
            skLineSegment(sketch, "E25.top", {"start": v(7.52, -2.31) * mm, "end": v(4.07, -2.31) * mm});
            skLineSegment(sketch, "E25.left", {"start": v(7.52, -1.56) * mm, "end": v(7.52, -2.31) * mm});
            skLineSegment(sketch, "E25.right", {"start": v(4.07, -1.56) * mm, "end": v(4.07, -2.31) * mm});
            skPoint(sketch, "E25.middle", {"position": v(5.8, -1.94) * mm});
            skPoint(sketch, "E25.middle.positionSnap0", {"position": v(5.8, -3.53) * mm});
            skPoint(sketch, "E25.centerSnap0", {"position": v(5.8, -3.53) * mm});
            skSolve(sketch);
        }
        {
            var Q0;
            Q0=makeQuery(id+"F65.imprint","IMPRINT",FACE,{"disambiguationData":[TD([[makeQuery(id+"F65.imprint","IMPRINT",EDGE,{"derivedFrom":sQuery(id+"F65.wireOp",EDGE,"E25.bottom")}),1.0]])]});
            extrude(context, id + "F66", {"entities" : qUnion([Q0]), "operationType" : NewBodyOperationType.ADD, "depth" : 3.37 * mm, "offsetDistance" : 25.4 * mm});
        }
        {
            var Q0;
            Q0=makeQuery(id+"F66.opExtrude","CAP_EDGE",EDGE,{"disambiguationData":[OSD([sQuery(id+"F65.wireOp",EDGE,"E25.left")])],"isStart":false});
            var Q1;
            Q1=makeQuery(id+"F66.opExtrude","CAP_EDGE",EDGE,{"disambiguationData":[OSD([sQuery(id+"F65.wireOp",EDGE,"E25.right")])],"isStart":false});
            fillet(context, id + "F67", {"entities" : qUnion([Q0, Q1]), "radius" : 1.93 * mm, "tangentPropagation" : true, "allowEdgeOverflow" : false});
        }
        {
            var Q0;
            Q0=makeQuery(id+"F66.opExtrude","SWEPT_FACE",FACE,{"disambiguationData":[OSD([sQuery(id+"F65.wireOp",EDGE,"E25.top")])]});
            var sketch = newSketch(context, id + "F68", { "sketchPlane" : qUnion([Q0])});
            skCircle(sketch, "E26", {"center": v(5.8, 81.73) * mm, "radius": 1.43 * mm});
            skPoint(sketch, "E26.centerSnap0", {"position": v(5.8, 80.1) * mm});
            skSolve(sketch);
        }
        {
            var Q0;
            Q0=makeQuery(id+"F68.imprint","IMPRINT",FACE,{"disambiguationData":[TD([[makeQuery(id+"F68.imprint","IMPRINT",EDGE,{"derivedFrom":sQuery(id+"F68.wireOp",EDGE,"E26")}),1.0]])]});
            extrude(context, id + "F69", {"entities" : qUnion([Q0]), "operationType" : NewBodyOperationType.REMOVE, "oppositeDirection" : true, "depth" : 40.57 * mm, "offsetDistance" : 25.4 * mm});
        }
        {
            var Q0;
            {var subQ0=sQuery(id+"F16.wireOp",EDGE,"E3.right");Q0=makeQuery(id+"F34.imprint","IMPRINT",FACE,{"disambiguationData":[TD([[makeQuery(id+"F34.imprint","IMPRINT",EDGE,{"derivedFrom":makeQuery(id+"F19.opPattern","COPY",EDGE,{"derivedFrom":makeQuery(id+"F17.opExtrude","CAP_EDGE",EDGE,{"disambiguationData":[OSD([subQ0])],"isStart":false}),"instanceName":"1"})}),1.0]])]});}
            var sketch = newSketch(context, id + "F70", { "sketchPlane" : qUnion([Q0])});
            skCircle(sketch, "E27", {"center": v(-7.2, 2.85) * mm, "radius": 5.8 * mm});
            skSolve(sketch);
        }
        {
            var Q0;
            Q0=makeQuery(id+"F70.imprint","IMPRINT",FACE,{"disambiguationData":[TD([[makeQuery(id+"F70.imprint","IMPRINT",EDGE,{"derivedFrom":sQuery(id+"F70.wireOp",EDGE,"E27")}),1.0]])]});
            extrude(context, id + "F71", {"entities" : qUnion([Q0]), "operationType" : NewBodyOperationType.ADD, "depth" : 2.62 * mm, "offsetDistance" : 25.4 * mm});
        }
        {
            var Q0;
            Q0=makeQuery(id+"F71.opExtrude","CAP_FACE",FACE,{"disambiguationData":[OSD([sQuery(id+"F70.wireOp",EDGE,"E27")])],"isStart":false});
            var sketch = newSketch(context, id + "F72", { "sketchPlane" : qUnion([Q0])});
            skCircle(sketch, "E28", {"center": v(-7.2, 2.85) * mm, "radius": 5.85 * mm});
            skSolve(sketch);
        }
        {
            var Q0;
            Q0=makeQuery(id+"F72.imprint","IMPRINT",FACE,{"disambiguationData":[TD([[makeQuery(id+"F72.imprint","IMPRINT",EDGE,{"derivedFrom":makeQuery(id+"F71.opExtrude","CAP_EDGE",EDGE,{"disambiguationData":[OSD([sQuery(id+"F70.wireOp",EDGE,"E27")])],"isStart":false})}),1.0]])]});
            extrude(context, id + "F73", {"entities" : qUnion([Q0]), "depth" : 2.27 * mm, "offsetDistance" : 25.4 * mm});
        }
        {
            var Q0;
            Q0=makeQuery(id+"F73.opExtrude","CAP_EDGE",EDGE,{"disambiguationData":[OSD([sQuery(id+"F70.wireOp",EDGE,"E27")])],"isStart":false});
            fillet(context, id + "F74", {"entities" : qUnion([Q0]), "radius" : 5.08 * mm, "tangentPropagation" : true, "allowEdgeOverflow" : false});
        }
    });
